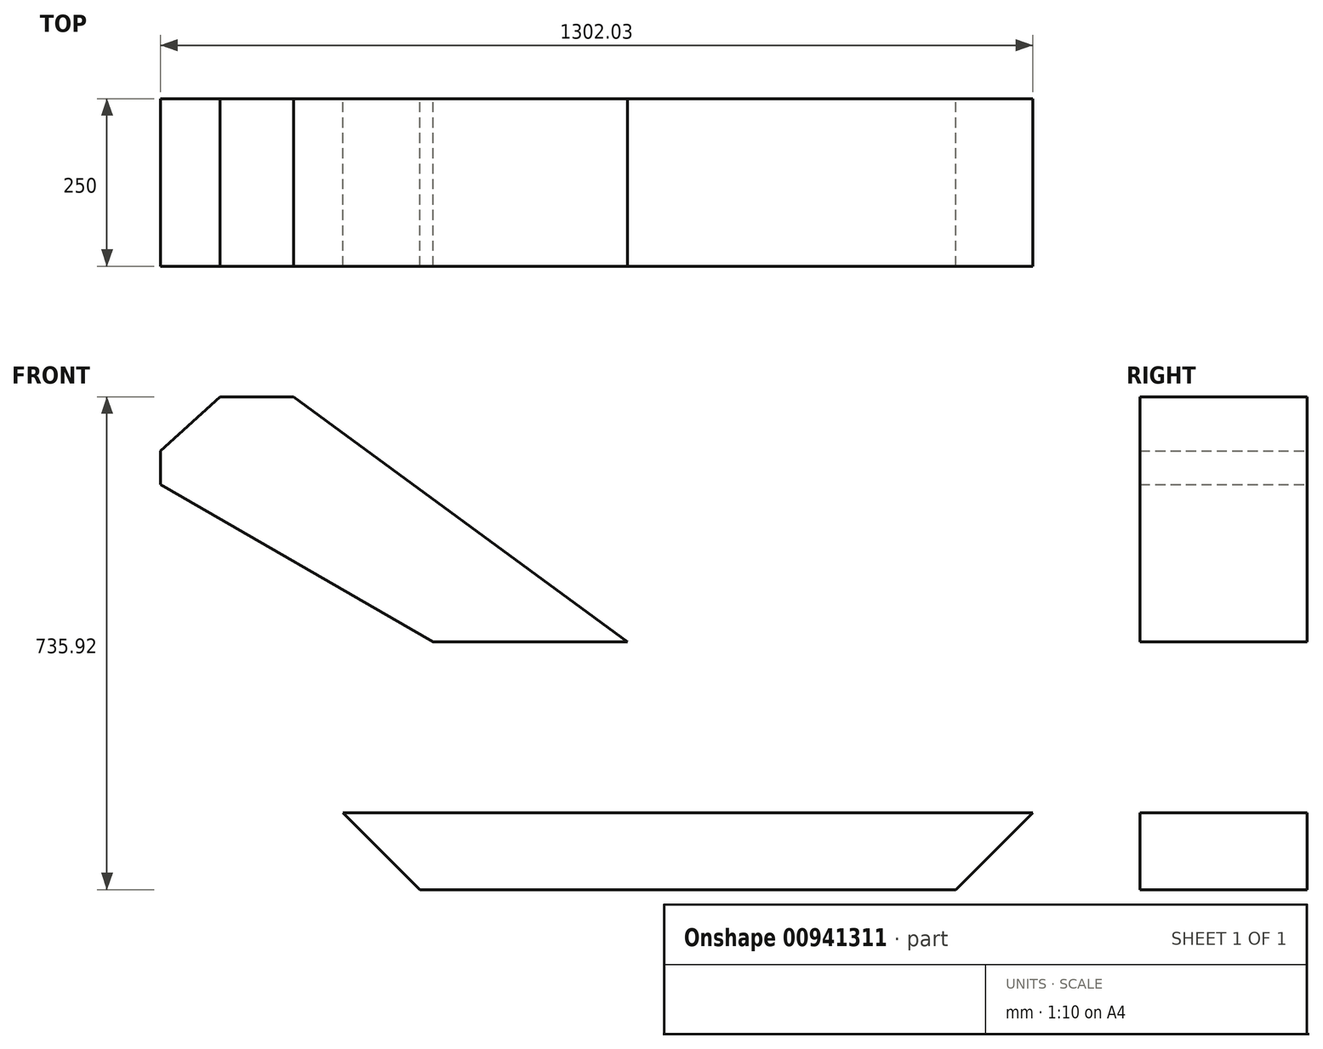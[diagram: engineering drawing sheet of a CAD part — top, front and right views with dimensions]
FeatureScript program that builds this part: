
annotation { "Feature Type Name" : "Feature", "Feature Type Description" : "" }
export const myFeature = defineFeature(function(context is Context, id is Id, definition is map)
    precondition{}
    {
        {
            var Q0;
            Q0=qCreatedBy(makeId("Front.planeOp"),FACE);
            var sketch = newSketch(context, id + "F0", { "sketchPlane" : qUnion([Q0])});
            skLineSegment(sketch, "E0", {"start": v(0, 0) * mm, "end": v(1030, 0) * mm});
            skLineSegment(sketch, "E1", {"start": v(1030, 0) * mm, "end": v(915, -115) * mm});
            skLineSegment(sketch, "E2", {"start": v(915, -115) * mm, "end": v(115, -115) * mm});
            skLineSegment(sketch, "E3", {"start": v(0, 0) * mm, "end": v(115, -115) * mm});
            skLineSegment(sketch, "E4", {"start": v(135, 255) * mm, "end": v(425, 255) * mm});
            skLineSegment(sketch, "E5", {"start": v(425, 255) * mm, "end": v(-73.42, 620.92) * mm});
            skLineSegment(sketch, "E6", {"start": v(-73.42, 620.92) * mm, "end": v(-183.42, 620.92) * mm});
            skLineSegment(sketch, "E7", {"start": v(-183.42, 620.92) * mm, "end": v(-272.03, 540) * mm});
            skLineSegment(sketch, "E8", {"start": v(-272.03, 540) * mm, "end": v(-272.03, 490) * mm});
            skLineSegment(sketch, "E9", {"start": v(-272.03, 490) * mm, "end": v(135, 255) * mm});
            skLineSegment(sketch, "E10", {"start": v(444.36, 620.92) * mm, "end": v(-427.85, 620.92) * mm, "construction": true});
            skSolve(sketch);
        }
        {
            var Q0;
            Q0 = qSketchRegion(id + "F0", true);
            extrude(context, id + "F1", {"entities" : qUnion([Q0]), "depth" : 250 * mm, "offsetDistance" : 25 * mm});
        }
    });
